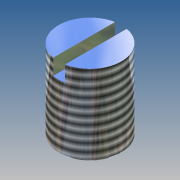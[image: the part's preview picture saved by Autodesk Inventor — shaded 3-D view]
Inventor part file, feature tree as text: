
AUTODESK INVENTOR PART (.ipt)
format: ipt  version: 2013 (Build 170138000, 138)  size: 129,024 bytes
history: native  units: mm (DEFAULTED — no unit token found)
features: extrude x2, sketch x2, chamfer x1, thread x1
ambient origin geometry x8: Origin, YZ Plane, XZ Plane, XY Plane, X Axis, Y Axis, Z Axis, Center Point
bodies: Solid1 (feature_tree)
feature tree (6):
  extrude  "Extrusion1"  Depth=10.3mm TaperAngle=0.0deg
  chamfer  "Chamfer1"  Distance=0.3mm
  thread  "Thread1"  [1 undecoded]
  extrude  "Extrusion2"  Depth=0.75mm
  sketch  "Sketch1"  dims[d0=8.0mm d1=10.3mm d2=0.0mm d3=0.3mm d4=0.3mm d5=10.0mm d6=0.0mm]
  sketch  "Sketch2"  dims[d7=1.5mm d8=0.75mm d9=2.0mm d10=0.0mm d11=45.0deg]
note: 1 required parameter value undecoded (feature->parameter linkage not recoverable at this tier; creation-order binding heuristic only, values carry confidence <= 0.55)
